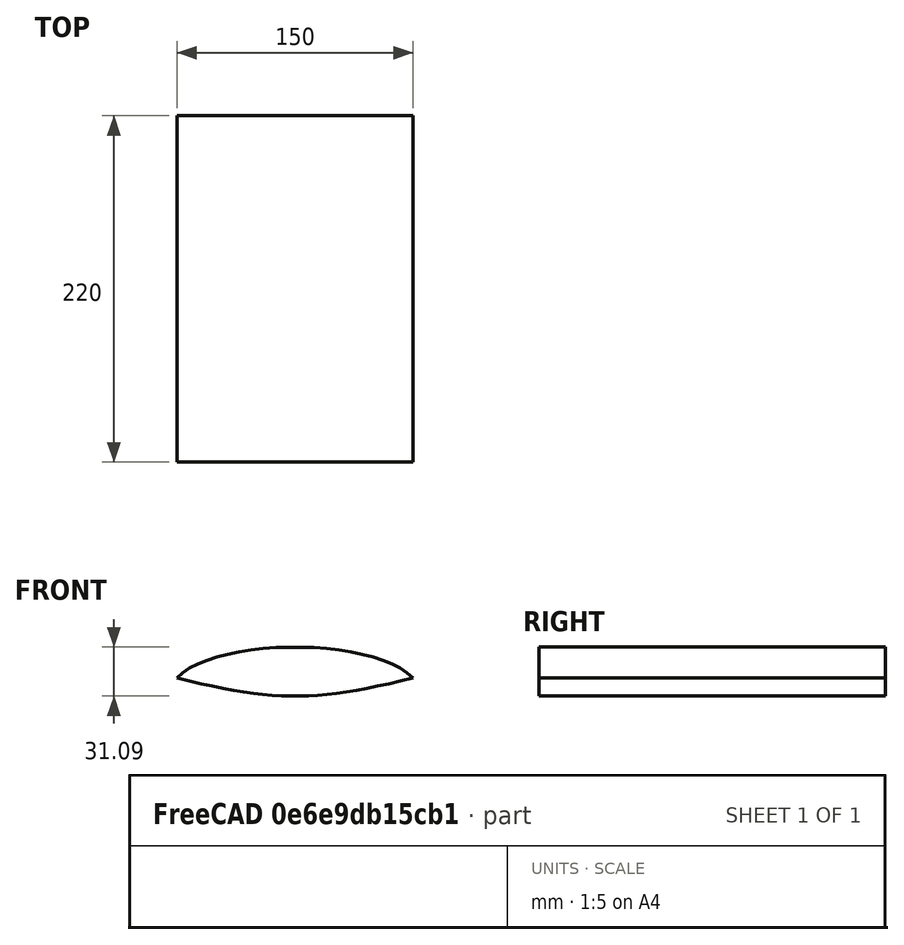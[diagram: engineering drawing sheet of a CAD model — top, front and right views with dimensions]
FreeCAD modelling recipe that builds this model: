
FCSTD DOCUMENT  (FreeCAD 0.20R7_voidlinux)
Label: Cad
License: All rights reserved
LicenseURL: http://en.wikipedia.org/wiki/All_rights_reserved
objects: Sketcher::SketchObject×3, PartDesign::Pad×1, PartDesign::Plane×1, PartDesign::Body×1
note: 7 computed .brp shape members not serialized (recipe doc carries the construction recipe); baked Part::Feature solids carry a one-line shape summary decoded from their .brp

FEATURE [Sketcher::SketchObject] Sketch  label="Body Profile"
  FullyConstrained = true
  MapMode = 5
  Placement = pos=(0,0,0) rot=(1,0,0;1.5708rad)
  Support = -> [XZ_Plane]
  sketch-geometry (14):
    g0-g3: Circle x4 (B-spline internal-alignment scaffolding for g4; pole/knot coordinates omitted)
    g4: BSplineCurve PolesCount=4 KnotsCount=2 Degree=3 IsPeriodic=0
    g5: GeomPoint X=-75 Y=0 Z=0
    g6: GeomPoint X=75 Y=0 Z=0
    g7-g10: Circle x4 (B-spline internal-alignment scaffolding for g11; pole/knot coordinates omitted)
    g11: BSplineCurve PolesCount=4 KnotsCount=2 Degree=3 IsPeriodic=0
    g12: GeomPoint X=-75 Y=0 Z=0
    g13: GeomPoint X=75 Y=0 Z=0
  constraints (25):
    c: Weight(g0) = 1
    c: PointOnObject(g4,g-1)
    c: Equal(g0,g1)
    c: Equal(g0,g2)
    c: Equal(g0,g3)
    c: InternalAlignment(g0-g3 -> g4) x4
    c: InternalAlignment(g5,g4)
    c: InternalAlignment(g6,g4)
    c: Weight(g7) = 1
    c: Coincident(g11,g4)
    c: Equal(g7,g8)
    c: Equal(g7,g9)
    c: Equal(g7,g10)
    c: Coincident(g11,g4)
    c: InternalAlignment(g7-g10 -> g11) x4
    c: InternalAlignment(g12,g11)
    c: InternalAlignment(g13,g11)
    c: Symmetric(g1,g2,g-2)
    c: Symmetric(g8,g9,g-2)
    c: Symmetric(g4,g4,g-2)
    c: DistanceX(g4,g4) = 150
    c: DistanceX(g1) = -49.6673
    c: DistanceY(g1) = 26.0447
    c: DistanceX(g8) = -13.3129
    c: DistanceY(g8) = -15.4125
FEATURE [PartDesign::Pad] Pad
  Direction = (0,-1,-2e-16)
  Length = 220
  Length2 = 10
  Placement = pos=(0,0,0) rot=(1,0,0;1.5708rad)
  Profile = -> Sketch
  ReferenceAxis = -> Sketch [N_Axis]
  Type = 0
FEATURE [Sketcher::SketchObject] Sketch001  label="Base"
  ExternalGeometry = -> [Pad]
  FullyConstrained = true
  MapMode = 5
  Placement = pos=(0,-220,0) rot=(1,0,0;1.5708rad)
  Support = -> [Pad]
FEATURE [PartDesign::Plane] DatumPlane
  AttachmentOffset = pos=(0,0,100) rot=(0,0,1;0rad)
  Length = 167.321
  MapMode = 5
  Placement = pos=(0,-320,2.22e-14) rot=(1,0,0;1.5708rad)
  ResizeMode = 0
  Support = -> [Pad]
  Width = 67.3205
FEATURE [Sketcher::SketchObject] Sketch002  label="Tip"
  FullyConstrained = true
  MapMode = 5
  Placement = pos=(0,-320,2.22e-14) rot=(1,0,0;1.5708rad)
  Support = -> [DatumPlane]
  sketch-geometry (1):
    g0: Circle CenterX=0 CenterY=0 CenterZ=0 NormalX=0 NormalY=0 NormalZ=1 AngleXU=0 Radius=1.5
  constraints (2):
    c: Coincident(g0,g-1)
    c: Radius(g0) = 1.5
FEATURE [PartDesign::Body] Body
  Group = -> [Sketch,Pad,Sketch001,DatumPlane,Sketch002]
  Origin = -> Origin
  Tip = -> Pad
